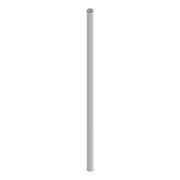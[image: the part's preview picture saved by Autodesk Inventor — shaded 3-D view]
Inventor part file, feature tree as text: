
AUTODESK INVENTOR PART (.ipt)
format: ipt  version: 2021 (Build 250183000, 183)  size: 83,456 bytes
history: native  units: mm
features: extrude x2, sketch x2, other x1
ambient origin geometry x8: Origin, YZ Plane, XZ Plane, XY Plane, X Axis, Y Axis, Z Axis, Center Point
bodies: Body1 (feature_tree)
feature tree (5):
  other  "Твердое тело1"
  extrude  "Выдавливание1"  Depth=1.0mm
  extrude  "Выдавливание2"  Depth=8.0mm
  sketch  "Эскиз1"
  sketch  "Эскиз2"
